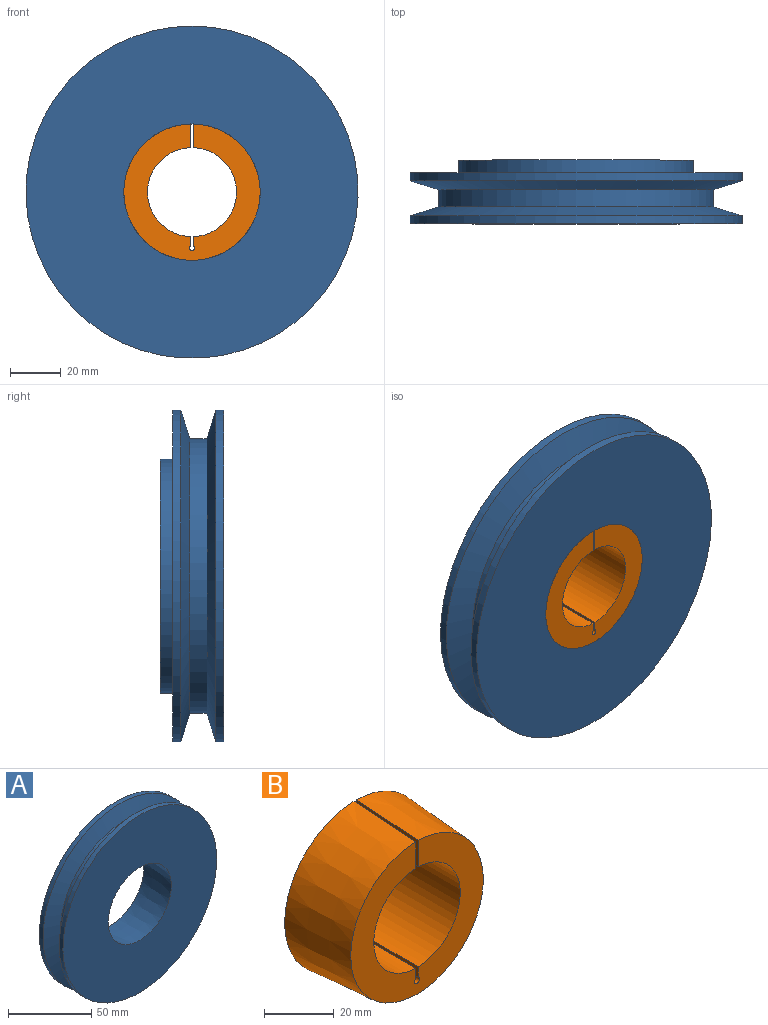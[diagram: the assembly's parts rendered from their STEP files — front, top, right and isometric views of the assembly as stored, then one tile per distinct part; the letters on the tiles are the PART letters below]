
ASSEMBLY  parts=2 mates=1
PART A: 10 faces, bbox 130.5x25x130.5 mm
  f0: cylinder r=46mm len=92mm, axis (0,1,0), area 1445.1mm2, adj f1,f8
  f1: plane 130.5x130.5mm, normal (0,1,0), area 6727.9mm2, adj f0,f2
  f2: cylinder r=65.25mm len=130.5mm, axis (0,1,0), area 1291.4mm2, adj f1,f3
  f3: cone r=54.05mm half-angle=73deg, axis (0,1,0), area 4389.5mm2, adj f2,f4
  f4: cylinder r=54.05mm len=108.1mm, axis (0,1,0), area 2326.9mm2, adj f3,f5
  f5: cone r=65.25mm half-angle=73deg, axis (0,-1,0), area 4389.5mm2, adj f4,f6
  f6: cylinder r=65.25mm len=130.5mm, axis (0,1,0), area 1291.4mm2, adj f5,f7
  f7: plane 130.5x130.5mm, normal (0,-1,0), area 11120.8mm2, adj f6,f9
  f8: plane 92x92mm, normal (0,1,0), area 4089mm2, adj f0,f9
  f9: cone r=26.79mm half-angle=4deg, axis (0,1,0), area 4356.1mm2, adj f7,f8
PART B: 10 faces, bbox 57.1x25x57.1 mm
  f0: cone r=26.79mm half-angle=4deg, axis (0,1,0), area 4331mm2, adj f1,f2,f5,f9
  f1: plane 57.08x57.07mm, normal (0,1,0), area 1578.8mm2, adj f0,f3,f4,f5,f6,f7,f8,f9
  f2: plane 53.58x53.58mm, normal (0,-1,0), area 1276.6mm2, adj f0,f3,f4,f5,f6,f7,f8,f9
  f3: cylinder r=17.5mm len=34.99mm, axis (0,1,0), area 1349.4mm2, adj f1,f2,f7,f9
  f4: cylinder r=17.5mm len=34.99mm, axis (0,1,0), area 1349.4mm2, adj f1,f2,f5,f6
  f5: plane 25x11.04mm, normal (-1,0,0), area 254.2mm2, adj f0,f1,f2,f4
  f6: plane 25x3.64mm, normal (-1,0,0), area 91mm2, adj f1,f2,f4,f8
  f7: plane 25x3.64mm, normal (1,0,0), area 91mm2, adj f1,f2,f3,f8
  f8: cylinder r=1mm len=25mm, axis (0,1,0), area 130.9mm2, adj f1,f2,f6,f7
  f9: plane 25x11.04mm, normal (1,0,0), area 254.2mm2, adj f0,f1,f2,f3
PLACE A at identity
PLACE B t=(0,-50,0)mm
MATE fastened A.f0 <-> B.f0  axis (0,-1,0) through (0,0,0)mm
